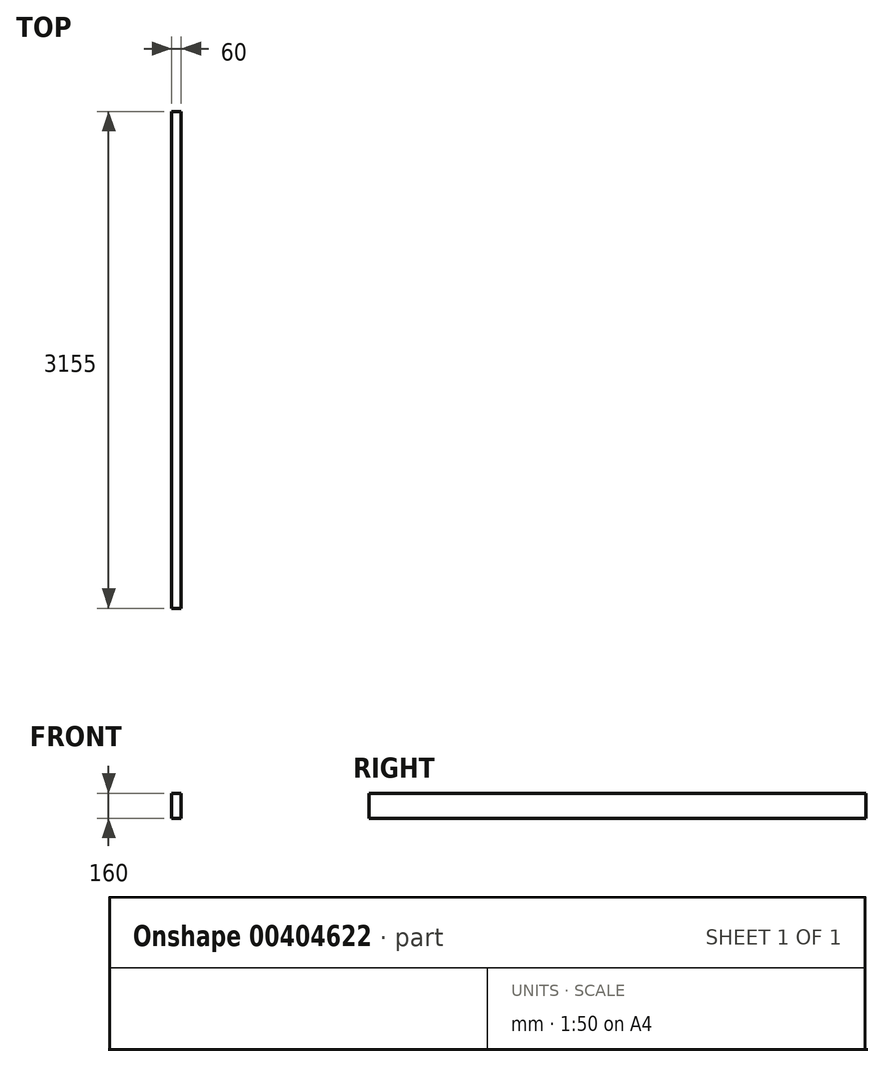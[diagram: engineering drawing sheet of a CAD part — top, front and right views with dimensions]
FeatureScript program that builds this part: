
annotation { "Feature Type Name" : "Feature", "Feature Type Description" : "" }
export const myFeature = defineFeature(function(context is Context, id is Id, definition is map)
    precondition{}
    {
        {
            var Q0;
            Q0=qCreatedBy(makeId("Front.planeOp"),FACE);
            var sketch = newSketch(context, id + "F0", { "sketchPlane" : qUnion([Q0])});
            skLineSegment(sketch, "E0.bottom", {"start": v(-30, 80) * mm, "end": v(30, 80) * mm});
            skLineSegment(sketch, "E0.top", {"start": v(-30, -80) * mm, "end": v(30, -80) * mm});
            skLineSegment(sketch, "E0.left", {"start": v(-30, 80) * mm, "end": v(-30, -80) * mm});
            skLineSegment(sketch, "E0.right", {"start": v(30, 80) * mm, "end": v(30, -80) * mm});
            skSolve(sketch);
        }
        {
            var Q0;
            Q0 = qSketchRegion(id + "F0", true);
            extrude(context, id + "F1", {"entities" : qUnion([Q0]), "depth" : 3155 * mm});
        }
    });
